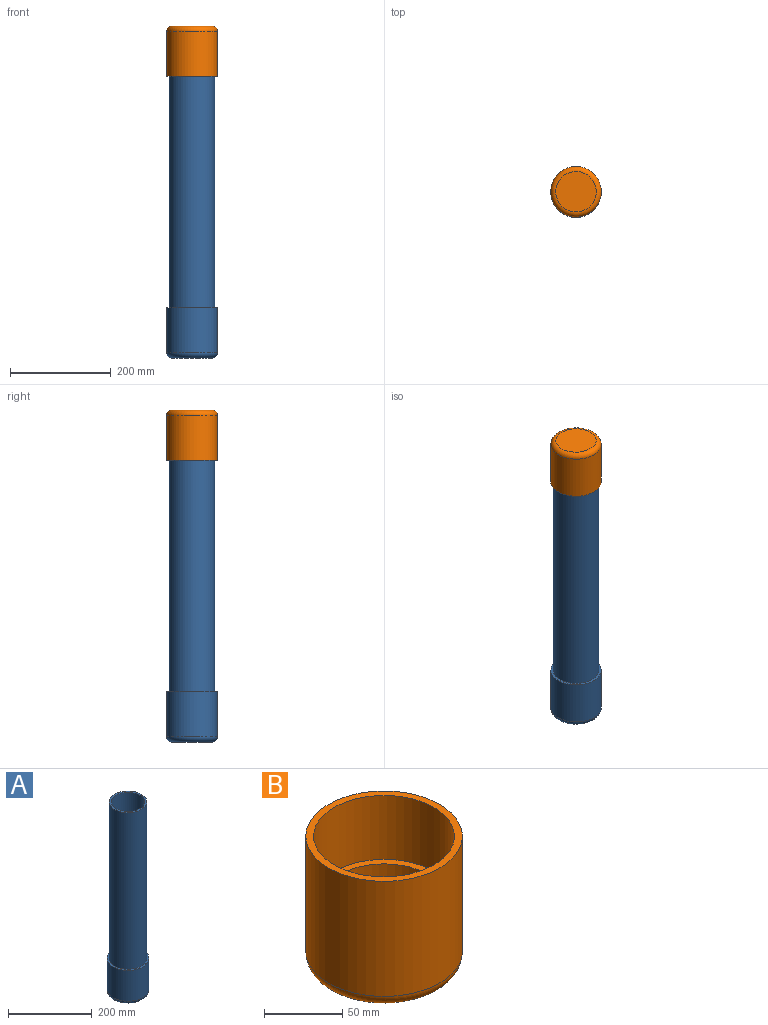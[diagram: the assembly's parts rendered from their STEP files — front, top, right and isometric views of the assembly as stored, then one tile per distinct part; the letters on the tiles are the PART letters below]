
ASSEMBLY  parts=2 mates=1
PART A: 8 faces, bbox 108.2x108.2x557.5 mm
  f0: plane 80x80mm, normal (0,0,-1), area 5026.5mm2, adj f3
  f1: cylinder r=50mm len=100mm, axis (0,0,-1), area 28274.3mm2, adj f2,f3
  f2: plane 100x100mm, normal (0,0,1), area 1492.3mm2, adj f1,f4
  f3: torus R=40mm, axis (0,0,1), area 4576.2mm2, adj f0,f1
  f4: cylinder r=45mm len=457.5mm, axis (0,0,-1), area 129355.1mm2, adj f2,f5
  f5: plane 90x90mm, normal (0,0,1), area 1335.2mm2, adj f4,f7
  f6: plane 80x80mm, normal (0,0,1), area 5026.5mm2, adj f7
  f7: cylinder r=40mm len=552.5mm, axis (0,0,-1), area 138858.4mm2, adj f5,f6
PART B: 8 faces, bbox 108.2x108.2x100 mm
  f0: cylinder r=40mm len=80mm, axis (0,0,-1), area 11309.7mm2, adj f1,f6
  f1: plane 90x90mm, normal (0,0,1), area 1335.2mm2, adj f0,f3
  f2: plane 80x80mm, normal (0,0,-1), area 5026.5mm2, adj f7
  f3: cylinder r=45mm len=90mm, axis (0,0,-1), area 14137.2mm2, adj f1,f5
  f4: cylinder r=50mm len=100mm, axis (0,0,-1), area 28274.3mm2, adj f5,f7
  f5: plane 100x100mm, normal (0,0,1), area 1492.3mm2, adj f3,f4
  f6: plane 80x80mm, normal (0,0,1), area 5026.5mm2, adj f0
  f7: torus R=40mm, axis (0,0,1), area 4576.2mm2, adj f2,f4
PLACE A t=(-130.75,-22.16,30)mm
PLACE B rot(axis=(1,0,0),180deg) t=(-130.75,-22.16,687.5)mm
MATE slider B.f0 <-> A.f1  axis (0,0,-1) through (-130.75,-22.16,587.5)mm
